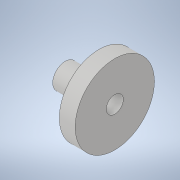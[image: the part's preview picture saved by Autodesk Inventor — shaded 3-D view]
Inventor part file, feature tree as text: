
AUTODESK INVENTOR PART (.ipt)
format: ipt  version: 2021 (Build 250183000, 183)  size: 107,008 bytes
history: native  units: in
note: dims shown in document units (in); Inventor stores cm internally (conversion verified against a paired STEP export)
features: extrude x2, sketch x2
ambient origin geometry x8: Origin, YZ Plane, XZ Plane, XY Plane, X Axis, Y Axis, Z Axis, Center Point
bodies: Solid1 (feature_tree)
feature tree (4):
  extrude  "Extrusion1"  Depth=0.268in
  extrude  "Extrusion2"  Depth=0.25in
  sketch  "Sketch1"  dims[d0=0.394in d1=0.268in]
  sketch  "Sketch2"  dims[d2=0.532in d3=0.0in d4=1.25in d5=0.25in d6=0.0in d7=0.268in]
